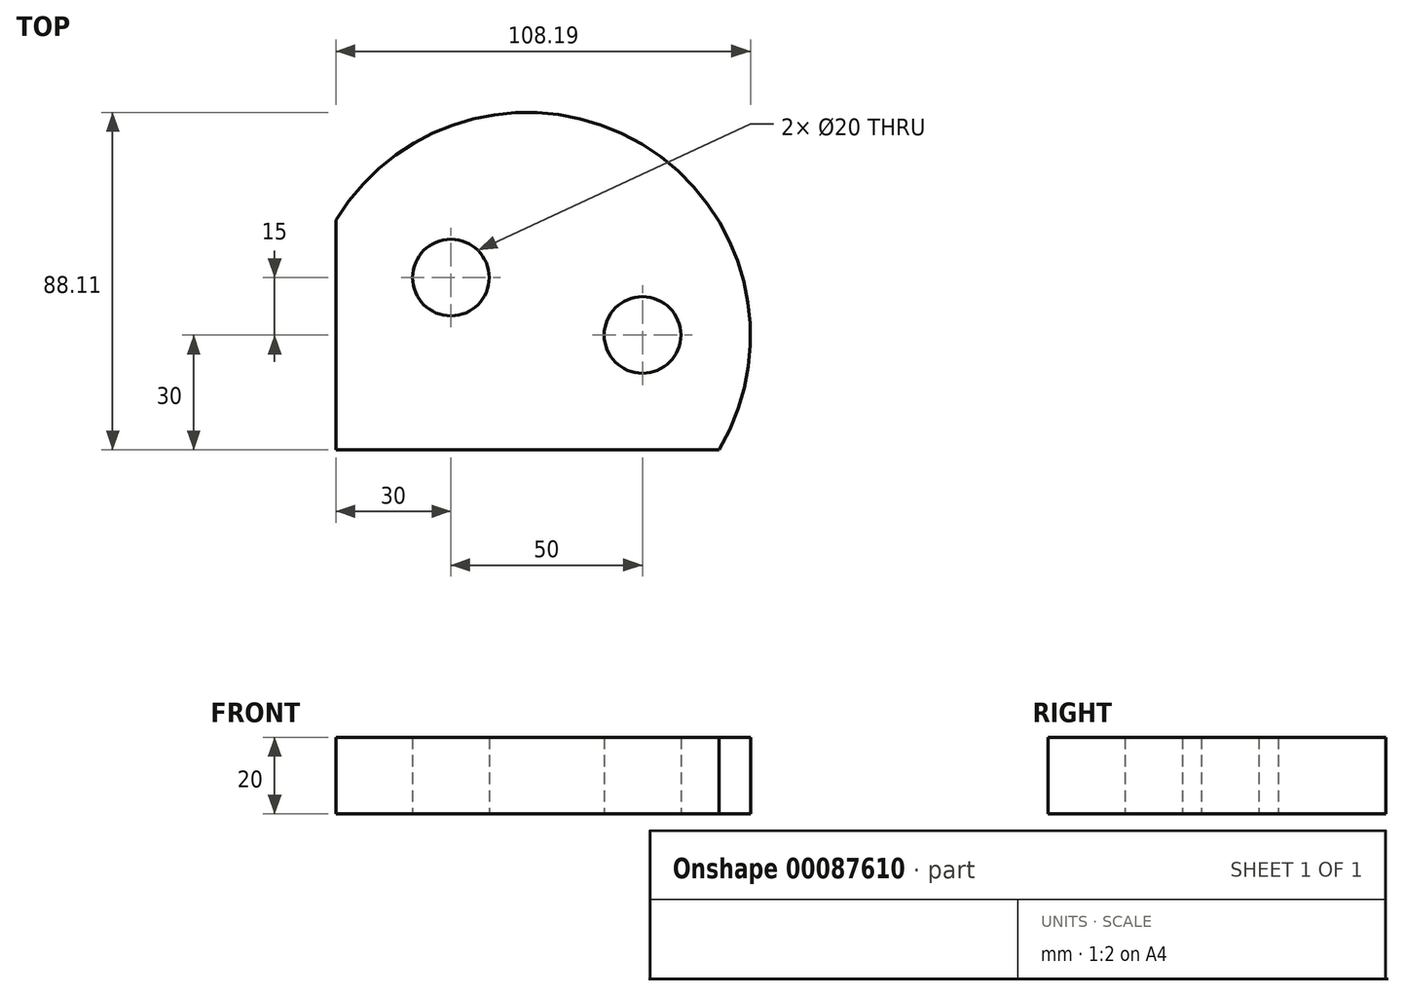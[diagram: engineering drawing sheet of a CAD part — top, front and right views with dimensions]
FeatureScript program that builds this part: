
annotation { "Feature Type Name" : "Feature", "Feature Type Description" : "" }
export const myFeature = defineFeature(function(context is Context, id is Id, definition is map)
    precondition{}
    {
        {
            var Q0;
            Q0=qCreatedBy(makeId("Top.planeOp"),FACE);
            var sketch = newSketch(context, id + "F0", { "sketchPlane" : qUnion([Q0])});
            skLineSegment(sketch, "E0", {"start": v(0, 0) * mm, "end": v(0, 60) * mm});
            skLineSegment(sketch, "E1", {"start": v(0, 0) * mm, "end": v(100, 0) * mm});
            skArc(sketch, "E2", {"start": v(100, 0) * mm, "mid": v(79.88, 79.8) * mm, "end": v(0, 60) * mm});
            skCircle(sketch, "E3", {"center": v(30, 45) * mm, "radius": 10 * mm});
            skCircle(sketch, "E4", {"center": v(80, 30) * mm, "radius": 10 * mm});
            skSolve(sketch);
        }
        {
            var Q0;
            Q0 = qSketchRegion(id + "F0", true);
            extrude(context, id + "F1", {"entities" : qUnion([Q0]), "depth" : 20 * mm});
        }
    });
